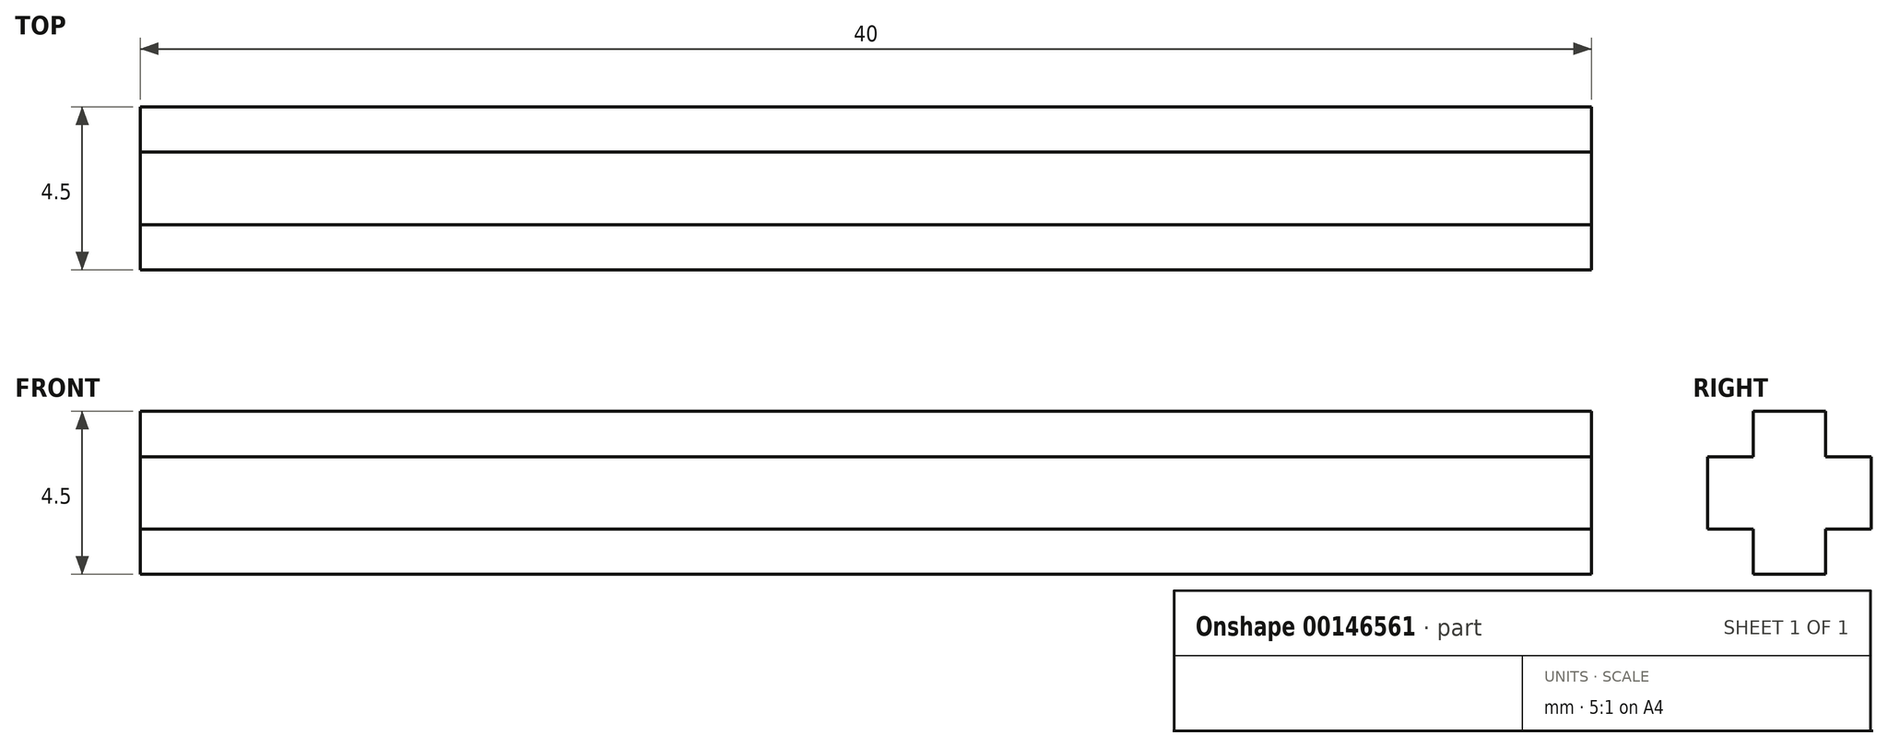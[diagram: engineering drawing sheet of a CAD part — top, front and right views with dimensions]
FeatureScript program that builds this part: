
annotation { "Feature Type Name" : "Feature", "Feature Type Description" : "" }
export const myFeature = defineFeature(function(context is Context, id is Id, definition is map)
    precondition{}
    {
        {
            var Q0;
            Q0=qCreatedBy(makeId("Front.planeOp"),FACE);
            var sketch = newSketch(context, id + "F0", { "sketchPlane" : qUnion([Q0])});
            skLineSegment(sketch, "E0", {"start": v(-20, 0) * mm, "end": v(20, 0) * mm});
            skSolve(sketch);
        }
        {
            var Q0;
            Q0=sQuery(id+"F0.wireOp",EDGE,"E0");
            var Q1;
            Q1=sQuery(id+"F0.wireOp",VERTEX,"E0.start");
            cPlane(context, id + "F1", {"entities" : qUnion([Q0, Q1]), "cplaneType" : CPlaneType.CURVE_POINT, "offset" : 25 * mm, "width" : 150 * mm, "height" : 150 * mm});
        }
        {
            var Q0;
            Q0=qCreatedBy(id+"F1.planeOp",FACE);
            var sketch = newSketch(context, id + "F2", { "sketchPlane" : qUnion([Q0])});
            skLineSegment(sketch, "E1.bottom", {"start": v(-1, -2.25) * mm, "end": v(1, -2.25) * mm});
            skLineSegment(sketch, "E1.top", {"start": v(-1, 2.25) * mm, "end": v(1, 2.25) * mm});
            skLineSegment(sketch, "E1.left", {"start": v(-1, -2.25) * mm, "end": v(-1, -1) * mm});
            skLineSegment(sketch, "E1.right", {"start": v(1, -2.25) * mm, "end": v(1, -1) * mm});
            skPoint(sketch, "E1.middle", {"position": v(0, 0) * mm});
            skLineSegment(sketch, "E2.bottom", {"start": v(-2.25, -1) * mm, "end": v(-1, -1) * mm});
            skLineSegment(sketch, "E2.top", {"start": v(-2.25, 1) * mm, "end": v(-1, 1) * mm});
            skLineSegment(sketch, "E2.left", {"start": v(-2.25, -1) * mm, "end": v(-2.25, 1) * mm});
            skLineSegment(sketch, "E2.right", {"start": v(2.25, -1) * mm, "end": v(2.25, 1) * mm});
            skLineSegment(sketch, "E3.trimOffspring", {"start": v(1, 1) * mm, "end": v(2.25, 1) * mm});
            skLineSegment(sketch, "E4.trimOffspring", {"start": v(1, 1) * mm, "end": v(1, 2.25) * mm});
            skLineSegment(sketch, "E5.trimOffspring", {"start": v(-1, 1) * mm, "end": v(-1, 2.25) * mm});
            skLineSegment(sketch, "E6.trimOffspring", {"start": v(1, -1) * mm, "end": v(2.25, -1) * mm});
            skSolve(sketch);
        }
        {
            var Q0;
            Q0=makeQuery(id+"F2.imprint","IMPRINT",FACE,{"disambiguationData":[TD([[makeQuery(id+"F2.imprint","IMPRINT",EDGE,{"derivedFrom":sQuery(id+"F2.wireOp",EDGE,"E1.bottom")}),1.0]])]});
            var Q1;
            Q1=sQuery(id+"F0.wireOp",EDGE,"E0");
            sweep(context, id + "F3", {"profiles" : qUnion([Q0]), "path" : qUnion([Q1])});
        }
    });
